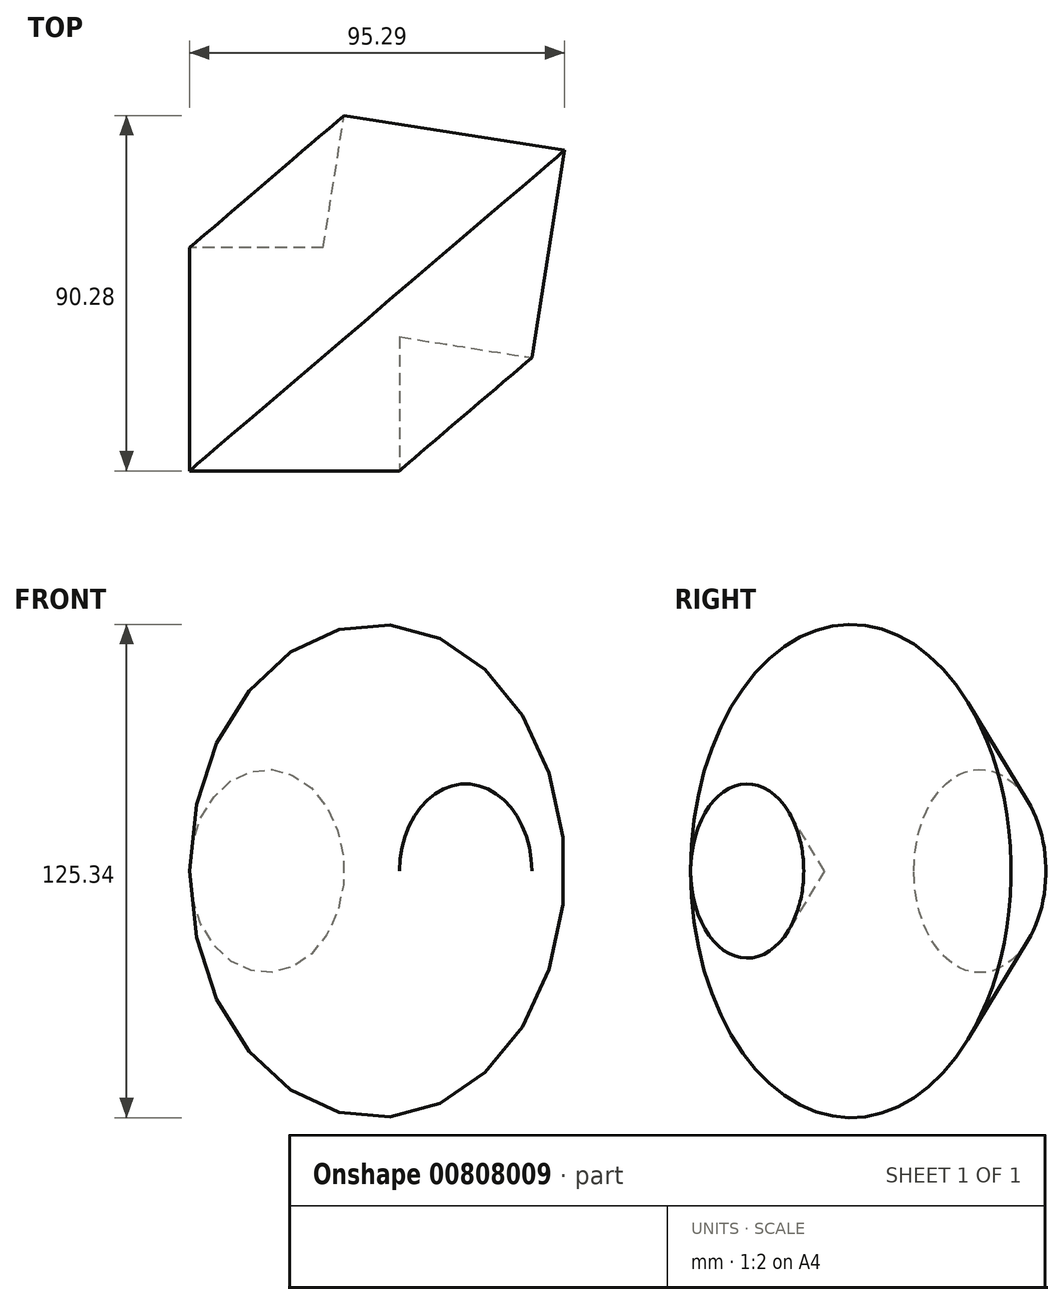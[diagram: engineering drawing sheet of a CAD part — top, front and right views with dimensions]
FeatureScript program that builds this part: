
annotation { "Feature Type Name" : "Feature", "Feature Type Description" : "" }
export const myFeature = defineFeature(function(context is Context, id is Id, definition is map)
    precondition{}
    {
        {
            var Q0;
            Q0=qCreatedBy(makeId("Top.planeOp"),FACE);
            var sketch = newSketch(context, id + "F0", { "sketchPlane" : qUnion([Q0])});
            skLineSegment(sketch, "E0.bottom", {"start": v(-25.85, 38.05) * mm, "end": v(27.5, 38.05) * mm});
            skLineSegment(sketch, "E0.top", {"start": v(-25.85, -18.67) * mm, "end": v(27.5, -18.67) * mm});
            skLineSegment(sketch, "E0.left", {"start": v(-25.85, 38.05) * mm, "end": v(-25.85, -18.67) * mm});
            skLineSegment(sketch, "E0.right", {"start": v(27.5, 38.05) * mm, "end": v(27.5, -18.67) * mm});
            skLineSegment(sketch, "E1", {"start": v(0, 47.55) * mm, "end": v(33, 8.93) * mm});
            skSolve(sketch);
        }
        {
            var Q0;
            {var subQ1=sQuery(id+"F0.wireOp",EDGE,"E0.top");Q0=makeQuery(id+"F0.imprint","IMPRINT",FACE,{"disambiguationData":[TD([[makeQuery(id+"F0.imprint","IMPRINT",EDGE,{"derivedFrom":subQ1}),1.0]])]});}
            var Q1;
            Q1=sQuery(id+"F0.wireOp",EDGE,"E1");
            revolve(context, id + "F1", {"surfaceOperationType" : NewSurfaceOperationType.NEW, "entities" : qUnion([Q0]), "axis" : qUnion([Q1]), "revolveType" : RevolveType.FULL});
        }
    });
